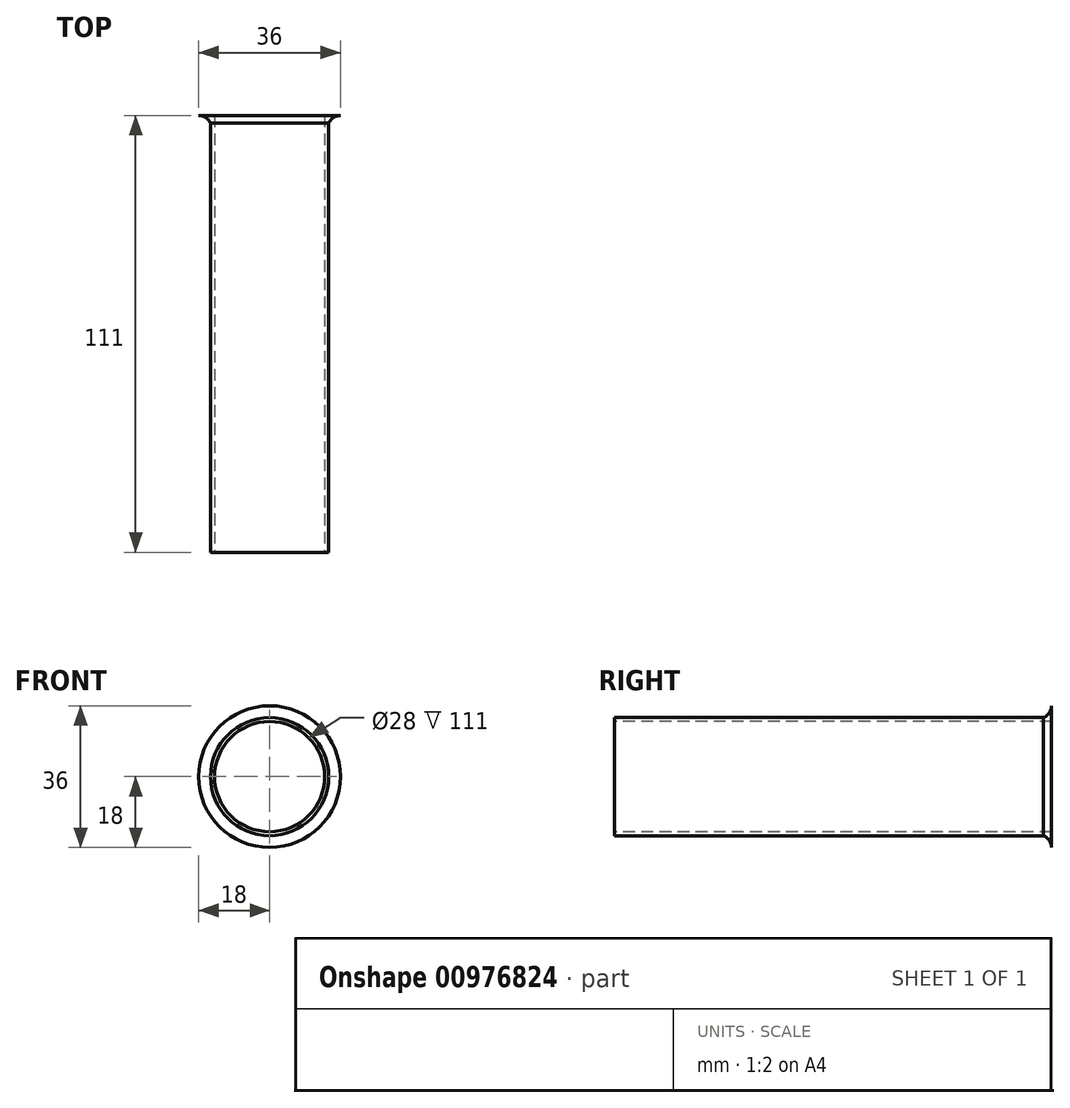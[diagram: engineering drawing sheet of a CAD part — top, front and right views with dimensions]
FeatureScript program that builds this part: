
annotation { "Feature Type Name" : "Feature", "Feature Type Description" : "" }
export const myFeature = defineFeature(function(context is Context, id is Id, definition is map)
    precondition{}
    {
        {
            var Q0;
            Q0=qCreatedBy(makeId("Front.planeOp"),FACE);
            var sketch = newSketch(context, id + "F0", { "sketchPlane" : qUnion([Q0])});
            skCircle(sketch, "E0", {"center": v(0, 0) * mm, "radius": 15 * mm});
            skSolve(sketch);
        }
        {
            var Q0;
            Q0=makeQuery(id+"F0.imprint","IMPRINT",FACE,{"disambiguationData":[TD([[makeQuery(id+"F0.imprint","IMPRINT",EDGE,{"derivedFrom":sQuery(id+"F0.wireOp",EDGE,"E0")}),1.0]])]});
            extrude(context, id + "F1", {"entities" : qUnion([Q0]), "depth" : 111 * mm, "offsetDistance" : 25 * mm});
        }
        {
            var Q0;
            Q0=makeQuery(id+"F1.opExtrude","CAP_FACE",FACE,{"disambiguationData":[OSD([sQuery(id+"F0.wireOp",EDGE,"E0")])],"isStart":false});
            var sketch = newSketch(context, id + "F2", { "sketchPlane" : qUnion([Q0])});
            skCircle(sketch, "E1", {"center": v(0, 0) * mm, "radius": 14 * mm});
            skSolve(sketch);
        }
        {
            var Q0;
            Q0 = qSketchRegion(id + "F2", true);
            extrude(context, id + "F3", {"entities" : qUnion([Q0]), "operationType" : NewBodyOperationType.REMOVE, "oppositeDirection" : true, "depth" : 111 * mm, "offsetDistance" : 25 * mm});
        }
        {
            var Q0;
            Q0=qCreatedBy(makeId("Right.planeOp"),FACE);
            var sketch = newSketch(context, id + "F4", { "sketchPlane" : qUnion([Q0])});
            skLineSegment(sketch, "E2", {"start": v(0, 15) * mm, "end": v(-2, 15) * mm});
            skArc(sketch, "E3", {"start": v(-2, 15) * mm, "mid": v(-0.56, 16.2) * mm, "end": v(0, 18) * mm});
            skLineSegment(sketch, "E4", {"start": v(0, 18) * mm, "end": v(0, 15) * mm});
            skSolve(sketch);
        }
        {
            var Q0;
            Q0 = qSketchRegion(id + "F4", true);
            var Q1;
            Q1=makeQuery(id+"F3.boolean.opBoolean","COPY",FACE,{"derivedFrom":makeQuery(id+"F3.opExtrude","SWEPT_FACE",FACE,{"disambiguationData":[OSD([sQuery(id+"F2.wireOp",EDGE,"E1")])]})});
            revolve(context, id + "F5", {"operationType" : NewBodyOperationType.ADD, "surfaceOperationType" : NewSurfaceOperationType.NEW, "entities" : qUnion([Q0]), "axis" : qUnion([Q1]), "revolveType" : RevolveType.FULL});
        }
    });
